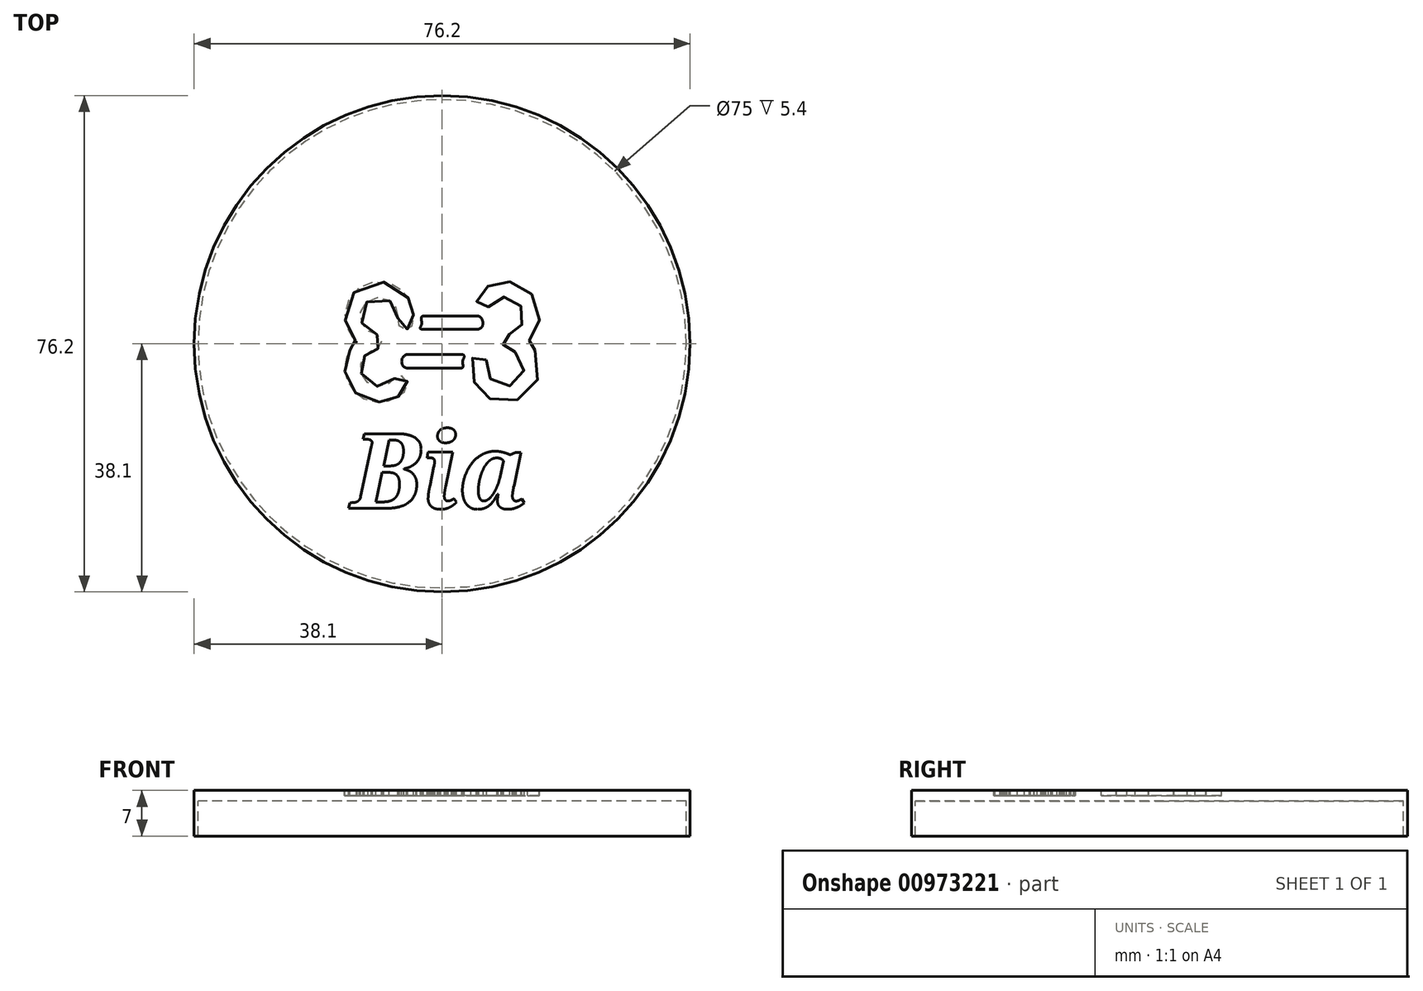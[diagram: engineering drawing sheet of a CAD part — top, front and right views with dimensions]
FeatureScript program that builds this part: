
annotation { "Feature Type Name" : "Feature", "Feature Type Description" : "" }
export const myFeature = defineFeature(function(context is Context, id is Id, definition is map)
    precondition{}
    {
        {
            var Q0;
            Q0=qCreatedBy(makeId("Top.planeOp"),FACE);
            var sketch = newSketch(context, id + "F0", { "sketchPlane" : qUnion([Q0])});
            skCircle(sketch, "E0", {"center": v(0, 0) * mm, "radius": 38.1 * mm});
            skLineSegment(sketch, "E1", {"start": v(-2.89, 4.28) * mm, "end": v(5.43, 4.28) * mm});
            skLineSegment(sketch, "E2", {"start": v(-3.2, 2.23) * mm, "end": v(5.56, 2.23) * mm});
            skFitSpline(sketch, "E3", {"points": [v(5.43, 4.28) * mm, v(6.26, 3.33) * mm, v(5.56, 2.23) * mm], "startDerivative": vector(3.46, -0.87) * mm, "endDerivative": vector(-3.8, -1.42) * mm});
            skFitSpline(sketch, "E4", {"points": [v(-3.2, 2.23) * mm, v(-3.36, 2.42) * mm, v(-3.2, 2.85) * mm, v(-3.12, 3.18) * mm, v(-3.2, 4.05) * mm, v(-2.89, 4.28) * mm], "startDerivative": vector(-1.6, 1) * mm, "endDerivative": vector(2.07, 0.77) * mm});
            skLineSegment(sketch, "E5", {"start": v(3.14, -1.65) * mm, "end": v(-5.46, -1.65) * mm});
            skLineSegment(sketch, "E6", {"start": v(-5.44, -3.73) * mm, "end": v(3, -3.73) * mm});
            skFitSpline(sketch, "E7", {"points": [v(3, -3.73) * mm, v(3.17, -3.63) * mm, v(3.2, -3.35) * mm, v(3.2, -2.4) * mm, v(3.37, -2.06) * mm, v(3.33, -1.76) * mm, v(3.14, -1.65) * mm], "startDerivative": vector(1.66, 0.56) * mm, "endDerivative": vector(-1.68, 0.57) * mm});
            skFitSpline(sketch, "E8", {"points": [v(-5.46, -1.65) * mm, v(-6.22, -2.67) * mm, v(-5.44, -3.73) * mm], "startDerivative": vector(-3.5, -1.64) * mm, "endDerivative": vector(3.92, -0.81) * mm});
            skCircle(sketch, "E9", {"center": v(0, 0) * mm, "radius": 37.5 * mm});
            skFitSpline(sketch, "E10", {"points": [v(-9.98, 1.4) * mm, v(-11.47, 1.98) * mm, v(-12.53, 4.02) * mm, v(-11.89, 6.13) * mm, v(-9.3, 7.11) * mm, v(-7.34, 5.88) * mm, v(-6.82, 4.42) * mm, v(-6.72, 2.96) * mm, v(-5.66, 2.23) * mm, v(-4.66, 2.7) * mm, v(-4.42, 4.05) * mm, v(-4.52, 5.25) * mm, v(-5.01, 6.72) * mm, v(-7.61, 9.14) * mm, v(-12.34, 8.86) * mm, v(-14.85, 5.3) * mm, v(-14.47, 2.1) * mm, v(-13.37, 0.53) * mm, v(-13.14, 0.3) * mm, v(-13.7, -0.28) * mm, v(-14.41, -1.42) * mm, v(-15, -3.7) * mm, v(-14.24, -6.34) * mm, v(-12.47, -8.2) * mm, v(-9.45, -8.95) * mm, v(-7.47, -8.5) * mm, v(-6.35, -7.78) * mm, v(-5.3, -6.47) * mm, v(-5.86, -5.1) * mm, v(-7.04, -5.1) * mm, v(-7.54, -5.6) * mm, v(-9.18, -6.51) * mm, v(-11.4, -6.01) * mm, v(-12.45, -4.47) * mm, v(-12.38, -2.6) * mm, v(-11.63, -1.58) * mm, v(-10.56, -0.97) * mm, v(-9.87, -0.77) * mm, v(-9.27, 0.36) * mm, v(-9.98, 1.4) * mm]});
            skFitSpline(sketch, "E11", {"points": [v(6.77, -2.48) * mm, v(5.64, -1.67) * mm, v(4.64, -2.22) * mm, v(4.65, -5.08) * mm, v(5.92, -7.33) * mm, v(8.05, -8.71) * mm, v(11.92, -8.48) * mm, v(14.63, -5.63) * mm, v(14.42, -1.33) * mm, v(13.3, 0.1) * mm, v(13.14, 0.3) * mm, v(13.47, 0.58) * mm, v(14.68, 2.5) * mm, v(14.7, 5.93) * mm, v(12.52, 8.73) * mm, v(9.85, 9.57) * mm, v(7.6, 9.1) * mm, v(5.6, 7.57) * mm, v(5.3, 6.43) * mm, v(5.85, 5.7) * mm, v(6.93, 5.59) * mm, v(8.28, 6.8) * mm, v(9.71, 7.17) * mm, v(11.49, 6.5) * mm, v(12.52, 4.86) * mm, v(12.36, 3.12) * mm, v(11.43, 1.97) * mm, v(10.47, 1.52) * mm, v(9.66, 1.18) * mm, v(9.31, 0.32) * mm, v(9.48, -0.42) * mm, v(10.25, -0.88) * mm, v(11.44, -1.4) * mm, v(12.57, -3.34) * mm, v(11.98, -5.47) * mm, v(9.98, -6.58) * mm, v(7.95, -5.98) * mm, v(6.85, -3.9) * mm, v(6.77, -2.48) * mm]});
            skText(sketch, "E12", { "text": "Bia", "fontName": "NotoSerif-BoldItalic.ttf"});
            const initialGuessF0  = {"E12": [-0.014, -0.02527, 1, 0, 0.01156]};
            skSetInitialGuess(sketch, initialGuessF0);
            skSolve(sketch);
        }
        {
            var Q0;
            Q0=makeQuery(id+"F0.imprint","IMPRINT",FACE,{"disambiguationData":[TD([[makeQuery(id+"F0.imprint","IMPRINT",EDGE,{"derivedFrom":sQuery(id+"F0.wireOp",EDGE,"E0")}),1.0]])]});
            extrude(context, id + "F1", {"entities" : qUnion([Q0]), "oppositeDirection" : true, "depth" : 7 * mm, "offsetDistance" : 25 * mm});
        }
        {
            var Q0;
            Q0=makeQuery(id+"F0.imprint","IMPRINT",FACE,{"disambiguationData":[TD([[makeQuery(id+"F0.imprint","IMPRINT",EDGE,{"derivedFrom":sQuery(id+"F0.wireOp",EDGE,"E1")}),1.0]])]});
            var Q1;
            Q1=makeQuery(id+"F0.imprint","IMPRINT",FACE,{"disambiguationData":[TD([[makeQuery(id+"F0.imprint","IMPRINT",EDGE,{"derivedFrom":sQuery(id+"F0.wireOp",EDGE,"466b3cb2-4dc8-4fe7-97b3-2f2f3c9f0260.sketch_text.stroke-0")}),-1.0]])]});
            var Q2;
            Q2=makeQuery(id+"F0.imprint","IMPRINT",FACE,{"disambiguationData":[TD([[makeQuery(id+"F0.imprint","IMPRINT",EDGE,{"derivedFrom":sQuery(id+"F0.wireOp",EDGE,"466b3cb2-4dc8-4fe7-97b3-2f2f3c9f0260.sketch_text.stroke-0")}),1.0]])]});
            var Q3;
            Q3=makeQuery(id+"F0.imprint","IMPRINT",FACE,{"disambiguationData":[TD([[makeQuery(id+"F0.imprint","IMPRINT",EDGE,{"derivedFrom":sQuery(id+"F0.wireOp",EDGE,"466b3cb2-4dc8-4fe7-97b3-2f2f3c9f0260.sketch_text.stroke-7")}),1.0]])]});
            var Q4;
            Q4=makeQuery(id+"F0.imprint","IMPRINT",FACE,{"disambiguationData":[TD([[makeQuery(id+"F0.imprint","IMPRINT",EDGE,{"derivedFrom":sQuery(id+"F0.wireOp",EDGE,"466b3cb2-4dc8-4fe7-97b3-2f2f3c9f0260.sketch_text.stroke-29")}),-1.0]])]});
            var Q5;
            Q5=makeQuery(id+"F0.imprint","IMPRINT",FACE,{"disambiguationData":[TD([[makeQuery(id+"F0.imprint","IMPRINT",EDGE,{"derivedFrom":sQuery(id+"F0.wireOp",EDGE,"466b3cb2-4dc8-4fe7-97b3-2f2f3c9f0260.sketch_text.stroke-37")}),-1.0]])]});
            var Q6;
            Q6=makeQuery(id+"F0.imprint","IMPRINT",FACE,{"disambiguationData":[TD([[makeQuery(id+"F0.imprint","IMPRINT",EDGE,{"derivedFrom":sQuery(id+"F0.wireOp",EDGE,"466b3cb2-4dc8-4fe7-97b3-2f2f3c9f0260.sketch_text.stroke-59")}),1.0]])]});
            var Q7;
            Q7=makeQuery(id+"F0.imprint","IMPRINT",FACE,{"disambiguationData":[TD([[makeQuery(id+"F0.imprint","IMPRINT",EDGE,{"derivedFrom":sQuery(id+"F0.wireOp",EDGE,"466b3cb2-4dc8-4fe7-97b3-2f2f3c9f0260.sketch_text.stroke-45")}),-1.0]])]});
            var Q8;
            Q8=makeQuery(id+"F0.imprint","IMPRINT",FACE,{"disambiguationData":[TD([[makeQuery(id+"F0.imprint","IMPRINT",EDGE,{"derivedFrom":sQuery(id+"F0.wireOp",EDGE,"E11")}),1.0]])]});
            var Q9;
            Q9=makeQuery(id+"F0.imprint","IMPRINT",FACE,{"disambiguationData":[TD([[makeQuery(id+"F0.imprint","IMPRINT",EDGE,{"derivedFrom":sQuery(id+"F0.wireOp",EDGE,"E1")}),-1.0]])]});
            var Q10;
            Q10=makeQuery(id+"F0.imprint","IMPRINT",FACE,{"disambiguationData":[TD([[makeQuery(id+"F0.imprint","IMPRINT",EDGE,{"derivedFrom":sQuery(id+"F0.wireOp",EDGE,"E5")}),1.0]])]});
            var Q11;
            Q11=makeQuery(id+"F0.imprint","IMPRINT",FACE,{"disambiguationData":[TD([[makeQuery(id+"F0.imprint","IMPRINT",EDGE,{"derivedFrom":sQuery(id+"F0.wireOp",EDGE,"E10")}),1.0]])]});
            var Q12;
            Q12=makeQuery(id+"F0.imprint","IMPRINT",FACE,{"disambiguationData":[TD([[makeQuery(id+"F0.imprint","IMPRINT",EDGE,{"derivedFrom":sQuery(id+"F0.wireOp",EDGE,"E12.sketch_text.stroke-0")}),-1.0]])]});
            var Q13;
            Q13=makeQuery(id+"F0.imprint","IMPRINT",FACE,{"disambiguationData":[TD([[makeQuery(id+"F0.imprint","IMPRINT",EDGE,{"derivedFrom":sQuery(id+"F0.wireOp",EDGE,"E12.sketch_text.stroke-48")}),-1.0]])]});
            var Q14;
            Q14=makeQuery(id+"F0.imprint","IMPRINT",FACE,{"disambiguationData":[TD([[makeQuery(id+"F0.imprint","IMPRINT",EDGE,{"derivedFrom":sQuery(id+"F0.wireOp",EDGE,"E12.sketch_text.stroke-76")}),-1.0]])]});
            var Q15;
            Q15=makeQuery(id+"F0.imprint","IMPRINT",FACE,{"disambiguationData":[TD([[makeQuery(id+"F0.imprint","IMPRINT",EDGE,{"derivedFrom":sQuery(id+"F0.wireOp",EDGE,"E12.sketch_text.stroke-92")}),-1.0]])]});
            var Q16;
            Q16=makeQuery(id+"F0.imprint","IMPRINT",FACE,{"disambiguationData":[TD([[makeQuery(id+"F0.imprint","IMPRINT",EDGE,{"derivedFrom":sQuery(id+"F0.wireOp",EDGE,"E12.sketch_text.stroke-131")}),1.0]])]});
            var Q17;
            Q17=makeQuery(id+"F0.imprint","IMPRINT",FACE,{"disambiguationData":[TD([[makeQuery(id+"F0.imprint","IMPRINT",EDGE,{"derivedFrom":sQuery(id+"F0.wireOp",EDGE,"E12.sketch_text.stroke-32")}),1.0]])]});
            var Q18;
            Q18=makeQuery(id+"F0.imprint","IMPRINT",FACE,{"disambiguationData":[TD([[makeQuery(id+"F0.imprint","IMPRINT",EDGE,{"derivedFrom":sQuery(id+"F0.wireOp",EDGE,"E12.sketch_text.stroke-41")}),1.0]])]});
            extrude(context, id + "F2", {"entities" : qUnion([Q0, Q1, Q2, Q3, Q4, Q5, Q6, Q7, Q8, Q9, Q10, Q11, Q12, Q13, Q14, Q15, Q16, Q17, Q18]), "operationType" : NewBodyOperationType.ADD, "oppositeDirection" : true, "depth" : 1.6 * mm, "offsetDistance" : 25 * mm});
        }
        {
            var Q0;
            Q0=makeQuery(id+"F0.imprint","IMPRINT",FACE,{"disambiguationData":[TD([[makeQuery(id+"F0.imprint","IMPRINT",EDGE,{"derivedFrom":sQuery(id+"F0.wireOp",EDGE,"E10")}),1.0]])]});
            var Q1;
            Q1=makeQuery(id+"F0.imprint","IMPRINT",FACE,{"disambiguationData":[TD([[makeQuery(id+"F0.imprint","IMPRINT",EDGE,{"derivedFrom":sQuery(id+"F0.wireOp",EDGE,"E5")}),1.0]])]});
            var Q2;
            Q2=makeQuery(id+"F0.imprint","IMPRINT",FACE,{"disambiguationData":[TD([[makeQuery(id+"F0.imprint","IMPRINT",EDGE,{"derivedFrom":sQuery(id+"F0.wireOp",EDGE,"E1")}),-1.0]])]});
            var Q3;
            Q3=makeQuery(id+"F0.imprint","IMPRINT",FACE,{"disambiguationData":[TD([[makeQuery(id+"F0.imprint","IMPRINT",EDGE,{"derivedFrom":sQuery(id+"F0.wireOp",EDGE,"E11")}),1.0]])]});
            var Q4;
            Q4=makeQuery(id+"F0.imprint","IMPRINT",FACE,{"disambiguationData":[TD([[makeQuery(id+"F0.imprint","IMPRINT",EDGE,{"derivedFrom":sQuery(id+"F0.wireOp",EDGE,"466b3cb2-4dc8-4fe7-97b3-2f2f3c9f0260.sketch_text.stroke-29")}),-1.0]])]});
            var Q5;
            Q5=makeQuery(id+"F0.imprint","IMPRINT",FACE,{"disambiguationData":[TD([[makeQuery(id+"F0.imprint","IMPRINT",EDGE,{"derivedFrom":sQuery(id+"F0.wireOp",EDGE,"466b3cb2-4dc8-4fe7-97b3-2f2f3c9f0260.sketch_text.stroke-37")}),-1.0]])]});
            var Q6;
            Q6=makeQuery(id+"F0.imprint","IMPRINT",FACE,{"disambiguationData":[TD([[makeQuery(id+"F0.imprint","IMPRINT",EDGE,{"derivedFrom":sQuery(id+"F0.wireOp",EDGE,"466b3cb2-4dc8-4fe7-97b3-2f2f3c9f0260.sketch_text.stroke-0")}),-1.0]])]});
            var Q7;
            Q7=makeQuery(id+"F0.imprint","IMPRINT",FACE,{"disambiguationData":[TD([[makeQuery(id+"F0.imprint","IMPRINT",EDGE,{"derivedFrom":sQuery(id+"F0.wireOp",EDGE,"466b3cb2-4dc8-4fe7-97b3-2f2f3c9f0260.sketch_text.stroke-45")}),-1.0]])]});
            var Q8;
            Q8=makeQuery(id+"F0.imprint","IMPRINT",FACE,{"disambiguationData":[TD([[makeQuery(id+"F0.imprint","IMPRINT",EDGE,{"derivedFrom":sQuery(id+"F0.wireOp",EDGE,"E12.sketch_text.stroke-0")}),-1.0]])]});
            var Q9;
            Q9=makeQuery(id+"F0.imprint","IMPRINT",FACE,{"disambiguationData":[TD([[makeQuery(id+"F0.imprint","IMPRINT",EDGE,{"derivedFrom":sQuery(id+"F0.wireOp",EDGE,"E12.sketch_text.stroke-48")}),-1.0]])]});
            var Q10;
            Q10=makeQuery(id+"F0.imprint","IMPRINT",FACE,{"disambiguationData":[TD([[makeQuery(id+"F0.imprint","IMPRINT",EDGE,{"derivedFrom":sQuery(id+"F0.wireOp",EDGE,"E12.sketch_text.stroke-76")}),-1.0]])]});
            var Q11;
            Q11=makeQuery(id+"F0.imprint","IMPRINT",FACE,{"disambiguationData":[TD([[makeQuery(id+"F0.imprint","IMPRINT",EDGE,{"derivedFrom":sQuery(id+"F0.wireOp",EDGE,"E12.sketch_text.stroke-92")}),-1.0]])]});
            extrude(context, id + "F3", {"entities" : qUnion([Q0, Q1, Q2, Q3, Q4, Q5, Q6, Q7, Q8, Q9, Q10, Q11]), "operationType" : NewBodyOperationType.REMOVE, "oppositeDirection" : true, "depth" : 0.8 * mm, "offsetDistance" : 25 * mm});
        }
        {
            var Q0;
            Q0=makeQuery(id+"F0.imprint","IMPRINT",FACE,{"disambiguationData":[TD([[makeQuery(id+"F0.imprint","IMPRINT",EDGE,{"derivedFrom":sQuery(id+"F0.wireOp",EDGE,"E12.sketch_text.stroke-0")}),-1.0]])]});
            var Q1;
            Q1=makeQuery(id+"F0.imprint","IMPRINT",FACE,{"disambiguationData":[TD([[makeQuery(id+"F0.imprint","IMPRINT",EDGE,{"derivedFrom":sQuery(id+"F0.wireOp",EDGE,"E12.sketch_text.stroke-48")}),-1.0]])]});
            var Q2;
            Q2=makeQuery(id+"F0.imprint","IMPRINT",FACE,{"disambiguationData":[TD([[makeQuery(id+"F0.imprint","IMPRINT",EDGE,{"derivedFrom":sQuery(id+"F0.wireOp",EDGE,"E12.sketch_text.stroke-76")}),-1.0]])]});
            var Q3;
            Q3=makeQuery(id+"F0.imprint","IMPRINT",FACE,{"disambiguationData":[TD([[makeQuery(id+"F0.imprint","IMPRINT",EDGE,{"derivedFrom":sQuery(id+"F0.wireOp",EDGE,"E12.sketch_text.stroke-92")}),-1.0]])]});
            extrude(context, id + "F4", {"entities" : qUnion([Q0, Q1, Q2, Q3]), "operationType" : NewBodyOperationType.REMOVE, "oppositeDirection" : true, "depth" : 0.2 * mm, "offsetDistance" : 25 * mm});
        }
    });
